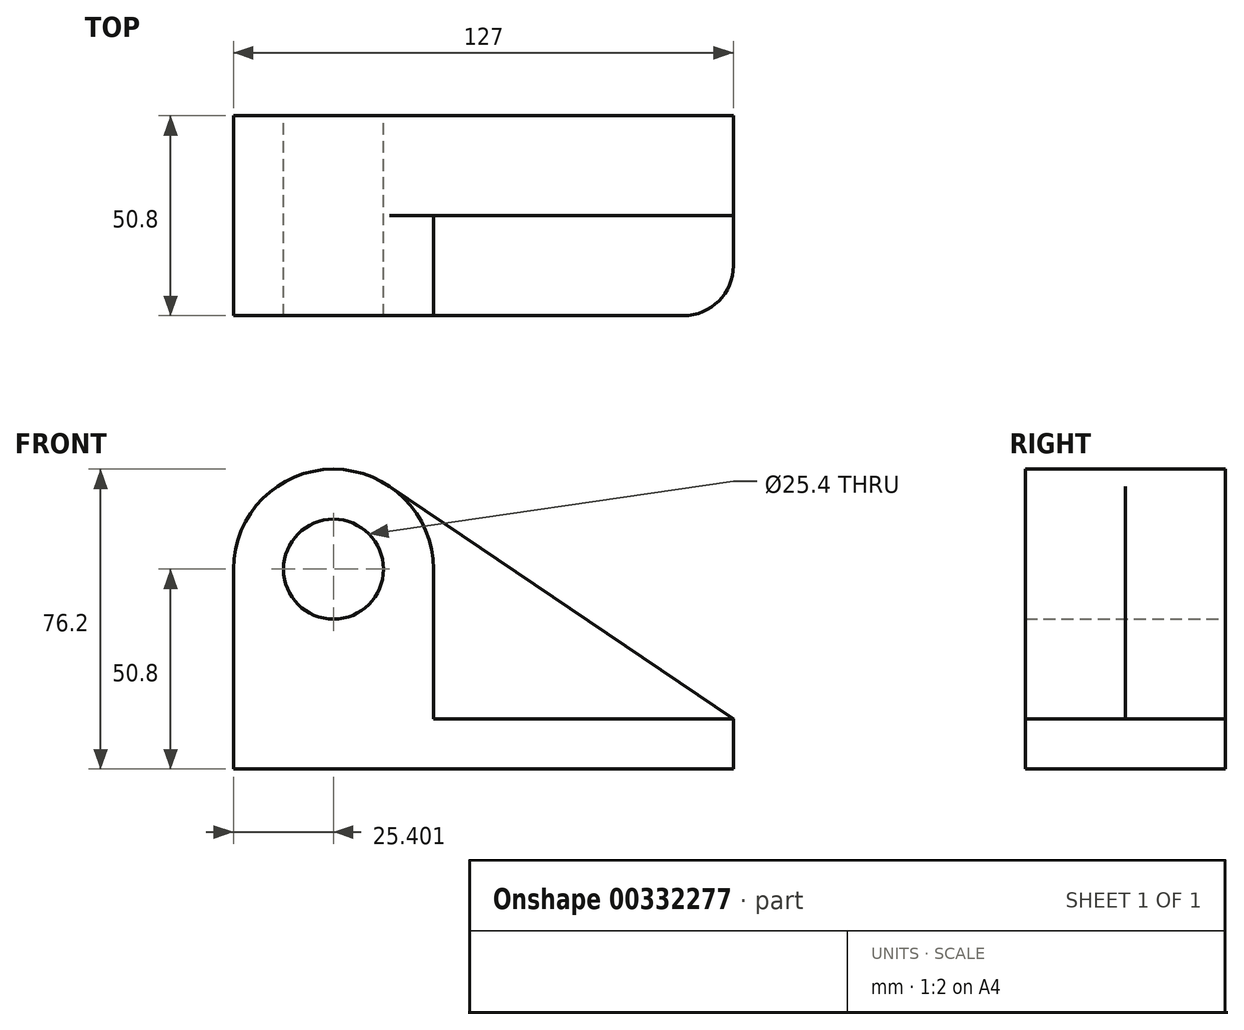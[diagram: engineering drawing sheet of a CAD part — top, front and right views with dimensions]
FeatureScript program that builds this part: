
annotation { "Feature Type Name" : "Feature", "Feature Type Description" : "" }
export const myFeature = defineFeature(function(context is Context, id is Id, definition is map)
    precondition{}
    {
        {
            var Q0;
            Q0=qCreatedBy(makeId("Front.planeOp"),FACE);
            var sketch = newSketch(context, id + "F0", { "sketchPlane" : qUnion([Q0])});
            skCircle(sketch, "E0", {"center": v(-36.3, 50.8) * mm, "radius": 12.7 * mm});
            skArc(sketch, "E1", {"start": v(-22.06, 71.83) * mm, "mid": v(-48.2, 73.24) * mm, "end": v(-61.7, 50.8) * mm});
            skLineSegment(sketch, "E2", {"start": v(-61.7, 50.8) * mm, "end": v(-61.7, 0) * mm});
            skLineSegment(sketch, "E3", {"start": v(-61.7, 0) * mm, "end": v(65.3, 0) * mm});
            skLineSegment(sketch, "E4", {"start": v(65.3, 0) * mm, "end": v(65.3, 12.7) * mm});
            skLineSegment(sketch, "E5", {"start": v(65.3, 12.7) * mm, "end": v(-22.06, 71.83) * mm});
            skSolve(sketch);
        }
        {
            var Q0;
            Q0 = qSketchRegion(id + "F0", true);
            extrude(context, id + "F1", {"entities" : qUnion([Q0]), "depth" : 25.4 * mm});
        }
        {
            var Q0;
            Q0=makeQuery(id+"F1.opExtrude","CAP_FACE",FACE,{"disambiguationData":[OSD([sQuery(id+"F0.wireOp",EDGE,"E0"),sQuery(id+"F0.wireOp",EDGE,"E1"),sQuery(id+"F0.wireOp",EDGE,"E2"),sQuery(id+"F0.wireOp",EDGE,"E3"),sQuery(id+"F0.wireOp",EDGE,"E4"),sQuery(id+"F0.wireOp",EDGE,"E5")])],"isStart":false});
            var sketch = newSketch(context, id + "F2", { "sketchPlane" : qUnion([Q0])});
            skCircle(sketch, "E6", {"center": v(-36.3, 50.8) * mm, "radius": 12.7 * mm});
            skArc(sketch, "E7", {"start": v(-10.9, 50.8) * mm, "mid": v(-36.3, 76.2) * mm, "end": v(-61.7, 50.8) * mm});
            skLineSegment(sketch, "E8.bottom", {"start": v(65.3, 12.7) * mm, "end": v(-10.9, 12.7) * mm});
            skLineSegment(sketch, "E8.top", {"start": v(65.3, 0) * mm, "end": v(-61.7, 0) * mm});
            skLineSegment(sketch, "E8.left", {"start": v(65.3, 12.7) * mm, "end": v(65.3, 0) * mm});
            skLineSegment(sketch, "E8.right", {"start": v(-61.7, 12.7) * mm, "end": v(-61.7, 0) * mm});
            skLineSegment(sketch, "E9", {"start": v(-61.7, 50.8) * mm, "end": v(-61.7, 3.41) * mm});
            skLineSegment(sketch, "E10", {"start": v(-10.9, 50.8) * mm, "end": v(-10.9, 12.7) * mm});
            skSolve(sketch);
        }
        {
            var Q0;
            Q0=makeQuery(id+"F2.imprint","IMPRINT",FACE,{"disambiguationData":[TD([[makeQuery(id+"F2.imprint","IMPRINT",EDGE,{"derivedFrom":sQuery(id+"F2.wireOp",EDGE,"E6")}),-1.0]])]});
            extrude(context, id + "F3", {"entities" : qUnion([Q0]), "operationType" : NewBodyOperationType.ADD, "depth" : 25.4 * mm});
        }
        {
            var Q0;
            Q0=makeQuery(id+"F3.opExtrude","CAP_EDGE",EDGE,{"disambiguationData":[OSD([sQuery(id+"F2.wireOp",EDGE,"E8.left")])],"isStart":false});
            fillet(context, id + "F4", {"entities" : qUnion([Q0]), "radius" : 12.7 * mm, "tangentPropagation" : true, "allowEdgeOverflow" : false});
        }
    });
